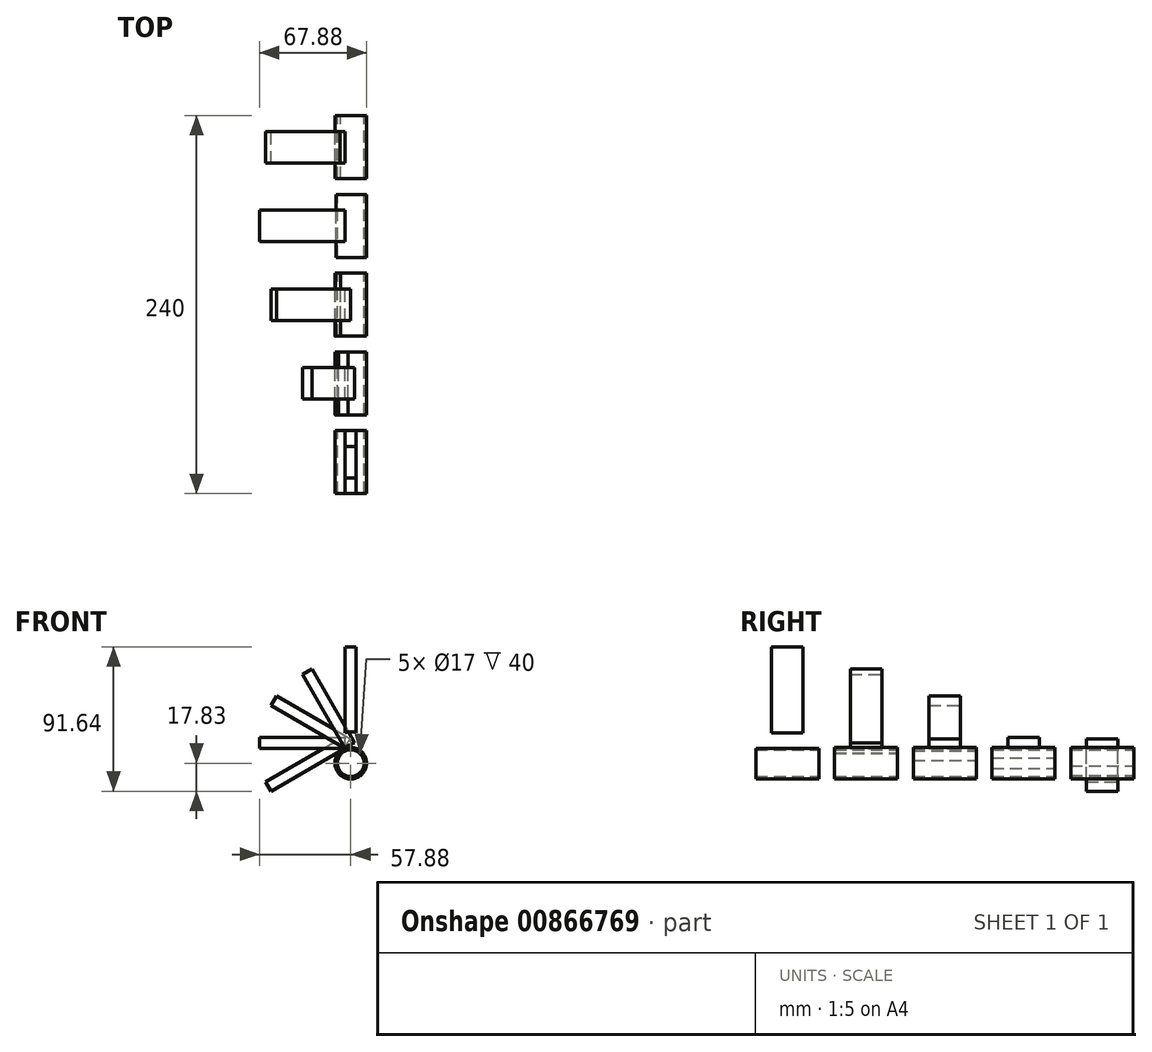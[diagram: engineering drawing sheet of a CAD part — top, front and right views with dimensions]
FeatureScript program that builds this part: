
annotation { "Feature Type Name" : "Feature", "Feature Type Description" : "" }
export const myFeature = defineFeature(function(context is Context, id is Id, definition is map)
    precondition{}
    {
        {
            var Q0;
            Q0=qCreatedBy(makeId("Front.planeOp"),FACE);
            var sketch = newSketch(context, id + "F0", { "sketchPlane" : qUnion([Q0])});
            skCircle(sketch, "E0", {"center": v(0, 0) * mm, "radius": 10 * mm});
            skCircle(sketch, "E1", {"center": v(0, 0) * mm, "radius": 8.5 * mm});
            skLineSegment(sketch, "E2.bottom", {"start": v(3.46, 63.8) * mm, "end": v(-3.46, 63.8) * mm});
            skLineSegment(sketch, "E2.top", {"start": v(3.46, 9.3) * mm, "end": v(-3.46, 9.3) * mm});
            skLineSegment(sketch, "E2.left", {"start": v(3.46, 63.8) * mm, "end": v(3.46, 9.3) * mm});
            skLineSegment(sketch, "E2.right", {"start": v(-3.46, 63.8) * mm, "end": v(-3.46, 9.3) * mm});
            skPoint(sketch, "E2.middle", {"position": v(0, 36.55) * mm});
            skSolve(sketch);
        }
        {
            var Q0;
            Q0=makeQuery(id+"F0.imprint","IMPRINT",FACE,{"disambiguationData":[TD([[makeQuery(id+"F0.imprint","IMPRINT",EDGE,{"derivedFrom":sQuery(id+"F0.wireOp",EDGE,"E1")}),-1.0]])]});
            var Q1;
            {var subQ5=sQuery(id+"F0.wireOp",EDGE,"E2.bottom");Q1=makeQuery(id+"F0.imprint","IMPRINT",FACE,{"disambiguationData":[TD([[makeQuery(id+"F0.imprint","IMPRINT",EDGE,{"derivedFrom":subQ5}),1.0]])]});}
            extrude(context, id + "F1", {"entities" : qUnion([Q0, Q1]), "endBound" : BoundingType.SYMMETRIC, "depth" : 20 * mm, "offsetDistance" : 25 * mm});
        }
        {
            var Q0;
            Q0=makeQuery(id+"F0.imprint","IMPRINT",FACE,{"disambiguationData":[TD([[makeQuery(id+"F0.imprint","IMPRINT",EDGE,{"derivedFrom":sQuery(id+"F0.wireOp",EDGE,"E1")}),-1.0]])]});
            extrude(context, id + "F2", {"entities" : qUnion([Q0]), "operationType" : NewBodyOperationType.ADD, "endBound" : BoundingType.SYMMETRIC, "depth" : 40 * mm, "offsetDistance" : 25 * mm});
        }
        {
            var Q0;
            Q0=makeQuery(id+"F1.opExtrude","SWEPT_BODY",BODY,{"disambiguationData":[OSD([sQuery(id+"F0.wireOp",EDGE,"E0"),sQuery(id+"F0.wireOp",EDGE,"E1"),sQuery(id+"F0.wireOp",EDGE,"E2.top"),sQuery(id+"F0.wireOp",EDGE,"E2.left"),sQuery(id+"F0.wireOp",EDGE,"E2.right")])]});
            transform(context, id + "F3", {"entities" : qUnion([Q0]), "transformType" : TransformType.TRANSLATION_3D, "dx" : 0 * mm, "dy" : 50 * mm, "dz" : 0 * mm, "makeCopy" : true});
        }
        {
            var Q0;
            Q0=makeQuery(id+"F3.opPattern","COPY",BODY,{"derivedFrom":makeQuery(id+"F1.opExtrude","SWEPT_BODY",BODY,{"disambiguationData":[OSD([sQuery(id+"F0.wireOp",EDGE,"E0"),sQuery(id+"F0.wireOp",EDGE,"E1"),sQuery(id+"F0.wireOp",EDGE,"E2.top"),sQuery(id+"F0.wireOp",EDGE,"E2.left"),sQuery(id+"F0.wireOp",EDGE,"E2.right")])]}),"instanceName":"1"});
            var Q1;
            {var subQ0=sQuery(id+"F0.wireOp",EDGE,"E1");Q1=makeQuery(id+"F3.opPattern","COPY",FACE,{"derivedFrom":makeQuery(id+"F2.boolean.opBoolean","MERGE",FACE,{"derivedFrom":[makeQuery(id+"F1.opExtrude","SWEPT_FACE",FACE,{"disambiguationData":[OSD([subQ0])]}),makeQuery(id+"F2.opExtrude","SWEPT_FACE",FACE,{"disambiguationData":[OSD([subQ0])]})]}),"instanceName":"1"});}
            transform(context, id + "F4", {"entities" : qUnion([Q0]), "transformType" : TransformType.ROTATION, "transformAxis" : qUnion([Q1]), "angle" : 30 * degree, "makeCopy" : false});
        }
        {
            var Q0;
            Q0=makeQuery(id+"F3.opPattern","COPY",BODY,{"derivedFrom":makeQuery(id+"F1.opExtrude","SWEPT_BODY",BODY,{"disambiguationData":[OSD([sQuery(id+"F0.wireOp",EDGE,"E0"),sQuery(id+"F0.wireOp",EDGE,"E1"),sQuery(id+"F0.wireOp",EDGE,"E2.top"),sQuery(id+"F0.wireOp",EDGE,"E2.left"),sQuery(id+"F0.wireOp",EDGE,"E2.right")])]}),"instanceName":"1"});
            transform(context, id + "F5", {"entities" : qUnion([Q0]), "transformType" : TransformType.TRANSLATION_3D, "dx" : 0 * mm, "dy" : 50 * mm, "dz" : 0 * mm, "makeCopy" : true});
        }
        {
            var Q0;
            Q0=makeQuery(id+"F5.opPattern","COPY",BODY,{"derivedFrom":makeQuery(id+"F3.opPattern","COPY",BODY,{"derivedFrom":makeQuery(id+"F1.opExtrude","SWEPT_BODY",BODY,{"disambiguationData":[OSD([sQuery(id+"F0.wireOp",EDGE,"E0"),sQuery(id+"F0.wireOp",EDGE,"E1"),sQuery(id+"F0.wireOp",EDGE,"E2.top"),sQuery(id+"F0.wireOp",EDGE,"E2.left"),sQuery(id+"F0.wireOp",EDGE,"E2.right")])]}),"instanceName":"1"}),"instanceName":"1"});
            var Q1;
            {var subQ0=sQuery(id+"F0.wireOp",EDGE,"E0");Q1=makeQuery(id+"F5.opPattern","COPY",FACE,{"derivedFrom":makeQuery(id+"F3.opPattern","COPY",FACE,{"derivedFrom":makeQuery(id+"F2.boolean.opBoolean","MERGE",FACE,{"derivedFrom":[makeQuery(id+"F1.opExtrude","SWEPT_FACE",FACE,{"disambiguationData":[OSD([subQ0]),TDD([makeQuery(id+"F0.imprint","IMPRINT",EDGE,{"disambiguationData":[TD([[makeQuery(id+"F0.imprint","INTERSECT",VERTEX,{"derivedFrom":[subQ0,sQuery(id+"F0.wireOp",EDGE,"E2.left")]}),1.0]])],"derivedFrom":subQ0})])]}),makeQuery(id+"F2.opExtrude","SWEPT_FACE",FACE,{"disambiguationData":[OSD([subQ0])]})]}),"instanceName":"1"}),"instanceName":"1"});}
            transform(context, id + "F6", {"entities" : qUnion([Q0]), "transformType" : TransformType.ROTATION, "transformAxis" : qUnion([Q1]), "angle" : 30 * degree, "oppositeDirection" : true, "makeCopy" : false});
        }
        {
            var Q0;
            Q0=makeQuery(id+"F5.opPattern","COPY",BODY,{"derivedFrom":makeQuery(id+"F3.opPattern","COPY",BODY,{"derivedFrom":makeQuery(id+"F1.opExtrude","SWEPT_BODY",BODY,{"disambiguationData":[OSD([sQuery(id+"F0.wireOp",EDGE,"E0"),sQuery(id+"F0.wireOp",EDGE,"E1"),sQuery(id+"F0.wireOp",EDGE,"E2.top"),sQuery(id+"F0.wireOp",EDGE,"E2.left"),sQuery(id+"F0.wireOp",EDGE,"E2.right")])]}),"instanceName":"1"}),"instanceName":"1"});
            transform(context, id + "F7", {"entities" : qUnion([Q0]), "transformType" : TransformType.TRANSLATION_3D, "dx" : 0 * mm, "dy" : 50 * mm, "dz" : 0 * mm, "makeCopy" : true});
        }
        {
            var Q0;
            Q0=makeQuery(id+"F7.opPattern","COPY",BODY,{"derivedFrom":makeQuery(id+"F5.opPattern","COPY",BODY,{"derivedFrom":makeQuery(id+"F3.opPattern","COPY",BODY,{"derivedFrom":makeQuery(id+"F1.opExtrude","SWEPT_BODY",BODY,{"disambiguationData":[OSD([sQuery(id+"F0.wireOp",EDGE,"E0"),sQuery(id+"F0.wireOp",EDGE,"E1"),sQuery(id+"F0.wireOp",EDGE,"E2.top"),sQuery(id+"F0.wireOp",EDGE,"E2.left"),sQuery(id+"F0.wireOp",EDGE,"E2.right")])]}),"instanceName":"1"}),"instanceName":"1"}),"instanceName":"1"});
            var Q1;
            {var subQ0=sQuery(id+"F0.wireOp",EDGE,"E1");Q1=makeQuery(id+"F7.opPattern","COPY",FACE,{"derivedFrom":makeQuery(id+"F5.opPattern","COPY",FACE,{"derivedFrom":makeQuery(id+"F3.opPattern","COPY",FACE,{"derivedFrom":makeQuery(id+"F2.boolean.opBoolean","MERGE",FACE,{"derivedFrom":[makeQuery(id+"F1.opExtrude","SWEPT_FACE",FACE,{"disambiguationData":[OSD([subQ0])]}),makeQuery(id+"F2.opExtrude","SWEPT_FACE",FACE,{"disambiguationData":[OSD([subQ0])]})]}),"instanceName":"1"}),"instanceName":"1"}),"instanceName":"1"});}
            transform(context, id + "F8", {"entities" : qUnion([Q0]), "transformType" : TransformType.ROTATION, "transformAxis" : qUnion([Q1]), "angle" : 30 * degree, "makeCopy" : false});
        }
        {
            var Q0;
            Q0=makeQuery(id+"F7.opPattern","COPY",BODY,{"derivedFrom":makeQuery(id+"F5.opPattern","COPY",BODY,{"derivedFrom":makeQuery(id+"F3.opPattern","COPY",BODY,{"derivedFrom":makeQuery(id+"F1.opExtrude","SWEPT_BODY",BODY,{"disambiguationData":[OSD([sQuery(id+"F0.wireOp",EDGE,"E0"),sQuery(id+"F0.wireOp",EDGE,"E1"),sQuery(id+"F0.wireOp",EDGE,"E2.top"),sQuery(id+"F0.wireOp",EDGE,"E2.left"),sQuery(id+"F0.wireOp",EDGE,"E2.right")])]}),"instanceName":"1"}),"instanceName":"1"}),"instanceName":"1"});
            transform(context, id + "F9", {"entities" : qUnion([Q0]), "transformType" : TransformType.TRANSLATION_3D, "dx" : 0 * mm, "dy" : 50 * mm, "dz" : 0 * mm, "makeCopy" : true});
        }
        {
            var Q0;
            Q0=makeQuery(id+"F9.opPattern","COPY",BODY,{"derivedFrom":makeQuery(id+"F7.opPattern","COPY",BODY,{"derivedFrom":makeQuery(id+"F5.opPattern","COPY",BODY,{"derivedFrom":makeQuery(id+"F3.opPattern","COPY",BODY,{"derivedFrom":makeQuery(id+"F1.opExtrude","SWEPT_BODY",BODY,{"disambiguationData":[OSD([sQuery(id+"F0.wireOp",EDGE,"E0"),sQuery(id+"F0.wireOp",EDGE,"E1"),sQuery(id+"F0.wireOp",EDGE,"E2.top"),sQuery(id+"F0.wireOp",EDGE,"E2.left"),sQuery(id+"F0.wireOp",EDGE,"E2.right")])]}),"instanceName":"1"}),"instanceName":"1"}),"instanceName":"1"}),"instanceName":"1"});
            var Q1;
            {var subQ0=sQuery(id+"F0.wireOp",EDGE,"E1");Q1=makeQuery(id+"F9.opPattern","COPY",FACE,{"derivedFrom":makeQuery(id+"F7.opPattern","COPY",FACE,{"derivedFrom":makeQuery(id+"F5.opPattern","COPY",FACE,{"derivedFrom":makeQuery(id+"F3.opPattern","COPY",FACE,{"derivedFrom":makeQuery(id+"F2.boolean.opBoolean","MERGE",FACE,{"derivedFrom":[makeQuery(id+"F1.opExtrude","SWEPT_FACE",FACE,{"disambiguationData":[OSD([subQ0])]}),makeQuery(id+"F2.opExtrude","SWEPT_FACE",FACE,{"disambiguationData":[OSD([subQ0])]})]}),"instanceName":"1"}),"instanceName":"1"}),"instanceName":"1"}),"instanceName":"1"});}
            transform(context, id + "F10", {"entities" : qUnion([Q0]), "transformType" : TransformType.ROTATION, "transformAxis" : qUnion([Q1]), "angle" : 30 * degree, "makeCopy" : false});
        }
        {
            var Q0;
            Q0=makeQuery(id+"F1.opExtrude","SWEPT_BODY",BODY,{"disambiguationData":[OSD([sQuery(id+"F0.wireOp",EDGE,"E0"),sQuery(id+"F0.wireOp",EDGE,"E2.bottom"),sQuery(id+"F0.wireOp",EDGE,"E2.left"),sQuery(id+"F0.wireOp",EDGE,"E2.right")])]});
            transform(context, id + "F11", {"entities" : qUnion([Q0]), "transformType" : TransformType.TRANSLATION_3D, "dx" : 0 * mm, "dy" : 50 * mm, "dz" : 0 * mm, "makeCopy" : true});
        }
        {
            var Q0;
            Q0=makeQuery(id+"F11.opPattern","COPY",BODY,{"derivedFrom":makeQuery(id+"F1.opExtrude","SWEPT_BODY",BODY,{"disambiguationData":[OSD([sQuery(id+"F0.wireOp",EDGE,"E0"),sQuery(id+"F0.wireOp",EDGE,"E2.bottom"),sQuery(id+"F0.wireOp",EDGE,"E2.left"),sQuery(id+"F0.wireOp",EDGE,"E2.right")])]}),"instanceName":"1"});
            var Q1;
            Q1=makeQuery(id+"F11.opPattern","COPY",EDGE,{"derivedFrom":makeQuery(id+"F1.opExtrude","SWEPT_EDGE",EDGE,{"disambiguationData":[OSD([sQuery(id+"F0.wireOp",EDGE,"E0"),sQuery(id+"F0.wireOp",EDGE,"E2.right")]),OD(0.0)]}),"instanceName":"1"});
            transform(context, id + "F12", {"entities" : qUnion([Q0]), "transformType" : TransformType.ROTATION, "transformAxis" : qUnion([Q1]), "angle" : 30 * degree, "oppositeDirection" : true, "makeCopy" : false});
        }
        {
            var Q0;
            Q0=makeQuery(id+"F11.opPattern","COPY",BODY,{"derivedFrom":makeQuery(id+"F1.opExtrude","SWEPT_BODY",BODY,{"disambiguationData":[OSD([sQuery(id+"F0.wireOp",EDGE,"E0"),sQuery(id+"F0.wireOp",EDGE,"E2.bottom"),sQuery(id+"F0.wireOp",EDGE,"E2.left"),sQuery(id+"F0.wireOp",EDGE,"E2.right")])]}),"instanceName":"1"});
            transform(context, id + "F13", {"entities" : qUnion([Q0]), "transformType" : TransformType.TRANSLATION_3D, "dx" : 0 * mm, "dy" : 50 * mm, "dz" : 0 * mm, "makeCopy" : true});
        }
        {
            var Q0;
            Q0=makeQuery(id+"F13.opPattern","COPY",BODY,{"derivedFrom":makeQuery(id+"F11.opPattern","COPY",BODY,{"derivedFrom":makeQuery(id+"F1.opExtrude","SWEPT_BODY",BODY,{"disambiguationData":[OSD([sQuery(id+"F0.wireOp",EDGE,"E0"),sQuery(id+"F0.wireOp",EDGE,"E2.bottom"),sQuery(id+"F0.wireOp",EDGE,"E2.left"),sQuery(id+"F0.wireOp",EDGE,"E2.right")])]}),"instanceName":"1"}),"instanceName":"1"});
            var Q1;
            Q1=makeQuery(id+"F13.opPattern","COPY",EDGE,{"derivedFrom":makeQuery(id+"F11.opPattern","COPY",EDGE,{"derivedFrom":makeQuery(id+"F1.opExtrude","SWEPT_EDGE",EDGE,{"disambiguationData":[OSD([sQuery(id+"F0.wireOp",EDGE,"E0"),sQuery(id+"F0.wireOp",EDGE,"E2.right")]),OD(0.0)]}),"instanceName":"1"}),"instanceName":"1"});
            transform(context, id + "F14", {"entities" : qUnion([Q0]), "transformType" : TransformType.ROTATION, "transformAxis" : qUnion([Q1]), "angle" : 30 * degree, "oppositeDirection" : true, "makeCopy" : false});
        }
        {
            var Q0;
            Q0=makeQuery(id+"F13.opPattern","COPY",BODY,{"derivedFrom":makeQuery(id+"F11.opPattern","COPY",BODY,{"derivedFrom":makeQuery(id+"F1.opExtrude","SWEPT_BODY",BODY,{"disambiguationData":[OSD([sQuery(id+"F0.wireOp",EDGE,"E0"),sQuery(id+"F0.wireOp",EDGE,"E2.bottom"),sQuery(id+"F0.wireOp",EDGE,"E2.left"),sQuery(id+"F0.wireOp",EDGE,"E2.right")])]}),"instanceName":"1"}),"instanceName":"1"});
            transform(context, id + "F15", {"entities" : qUnion([Q0]), "transformType" : TransformType.TRANSLATION_3D, "dx" : 0 * mm, "dy" : 50 * mm, "dz" : 0 * mm, "makeCopy" : true});
        }
        {
            var Q0;
            Q0=makeQuery(id+"F15.opPattern","COPY",BODY,{"derivedFrom":makeQuery(id+"F13.opPattern","COPY",BODY,{"derivedFrom":makeQuery(id+"F11.opPattern","COPY",BODY,{"derivedFrom":makeQuery(id+"F1.opExtrude","SWEPT_BODY",BODY,{"disambiguationData":[OSD([sQuery(id+"F0.wireOp",EDGE,"E0"),sQuery(id+"F0.wireOp",EDGE,"E2.bottom"),sQuery(id+"F0.wireOp",EDGE,"E2.left"),sQuery(id+"F0.wireOp",EDGE,"E2.right")])]}),"instanceName":"1"}),"instanceName":"1"}),"instanceName":"1"});
            var Q1;
            Q1=makeQuery(id+"F15.opPattern","COPY",EDGE,{"derivedFrom":makeQuery(id+"F13.opPattern","COPY",EDGE,{"derivedFrom":makeQuery(id+"F11.opPattern","COPY",EDGE,{"derivedFrom":makeQuery(id+"F1.opExtrude","SWEPT_EDGE",EDGE,{"disambiguationData":[OSD([sQuery(id+"F0.wireOp",EDGE,"E0"),sQuery(id+"F0.wireOp",EDGE,"E2.right")]),OD(0.0)]}),"instanceName":"1"}),"instanceName":"1"}),"instanceName":"1"});
            transform(context, id + "F16", {"entities" : qUnion([Q0]), "transformType" : TransformType.ROTATION, "transformAxis" : qUnion([Q1]), "angle" : 30 * degree, "oppositeDirection" : true, "makeCopy" : false});
        }
        {
            var Q0;
            Q0=makeQuery(id+"F15.opPattern","COPY",BODY,{"derivedFrom":makeQuery(id+"F13.opPattern","COPY",BODY,{"derivedFrom":makeQuery(id+"F11.opPattern","COPY",BODY,{"derivedFrom":makeQuery(id+"F1.opExtrude","SWEPT_BODY",BODY,{"disambiguationData":[OSD([sQuery(id+"F0.wireOp",EDGE,"E0"),sQuery(id+"F0.wireOp",EDGE,"E2.bottom"),sQuery(id+"F0.wireOp",EDGE,"E2.left"),sQuery(id+"F0.wireOp",EDGE,"E2.right")])]}),"instanceName":"1"}),"instanceName":"1"}),"instanceName":"1"});
            transform(context, id + "F17", {"entities" : qUnion([Q0]), "transformType" : TransformType.TRANSLATION_3D, "dx" : 0 * mm, "dy" : 50 * mm, "dz" : 0 * mm, "makeCopy" : true});
        }
        {
            var Q0;
            Q0=makeQuery(id+"F17.opPattern","COPY",BODY,{"derivedFrom":makeQuery(id+"F15.opPattern","COPY",BODY,{"derivedFrom":makeQuery(id+"F13.opPattern","COPY",BODY,{"derivedFrom":makeQuery(id+"F11.opPattern","COPY",BODY,{"derivedFrom":makeQuery(id+"F1.opExtrude","SWEPT_BODY",BODY,{"disambiguationData":[OSD([sQuery(id+"F0.wireOp",EDGE,"E0"),sQuery(id+"F0.wireOp",EDGE,"E2.bottom"),sQuery(id+"F0.wireOp",EDGE,"E2.left"),sQuery(id+"F0.wireOp",EDGE,"E2.right")])]}),"instanceName":"1"}),"instanceName":"1"}),"instanceName":"1"}),"instanceName":"1"});
            var Q1;
            Q1=makeQuery(id+"F17.opPattern","COPY",EDGE,{"derivedFrom":makeQuery(id+"F15.opPattern","COPY",EDGE,{"derivedFrom":makeQuery(id+"F13.opPattern","COPY",EDGE,{"derivedFrom":makeQuery(id+"F11.opPattern","COPY",EDGE,{"derivedFrom":makeQuery(id+"F1.opExtrude","SWEPT_EDGE",EDGE,{"disambiguationData":[OSD([sQuery(id+"F0.wireOp",EDGE,"E0"),sQuery(id+"F0.wireOp",EDGE,"E2.right")]),OD(0.0)]}),"instanceName":"1"}),"instanceName":"1"}),"instanceName":"1"}),"instanceName":"1"});
            transform(context, id + "F18", {"entities" : qUnion([Q0]), "transformType" : TransformType.ROTATION, "transformAxis" : qUnion([Q1]), "angle" : 30 * degree, "oppositeDirection" : true, "makeCopy" : false});
        }
        {
            var Q0;
            Q0=makeQuery(id+"F1.opExtrude","SWEPT_BODY",BODY,{"disambiguationData":[OSD([sQuery(id+"F0.wireOp",EDGE,"E0"),sQuery(id+"F0.wireOp",EDGE,"E2.bottom"),sQuery(id+"F0.wireOp",EDGE,"E2.left"),sQuery(id+"F0.wireOp",EDGE,"E2.right")])]});
            transform(context, id + "F19", {"entities" : qUnion([Q0]), "transformType" : TransformType.TRANSLATION_3D, "dx" : 0 * mm, "dy" : 0 * mm, "dz" : 10 * mm, "makeCopy" : false});
        }
    });
